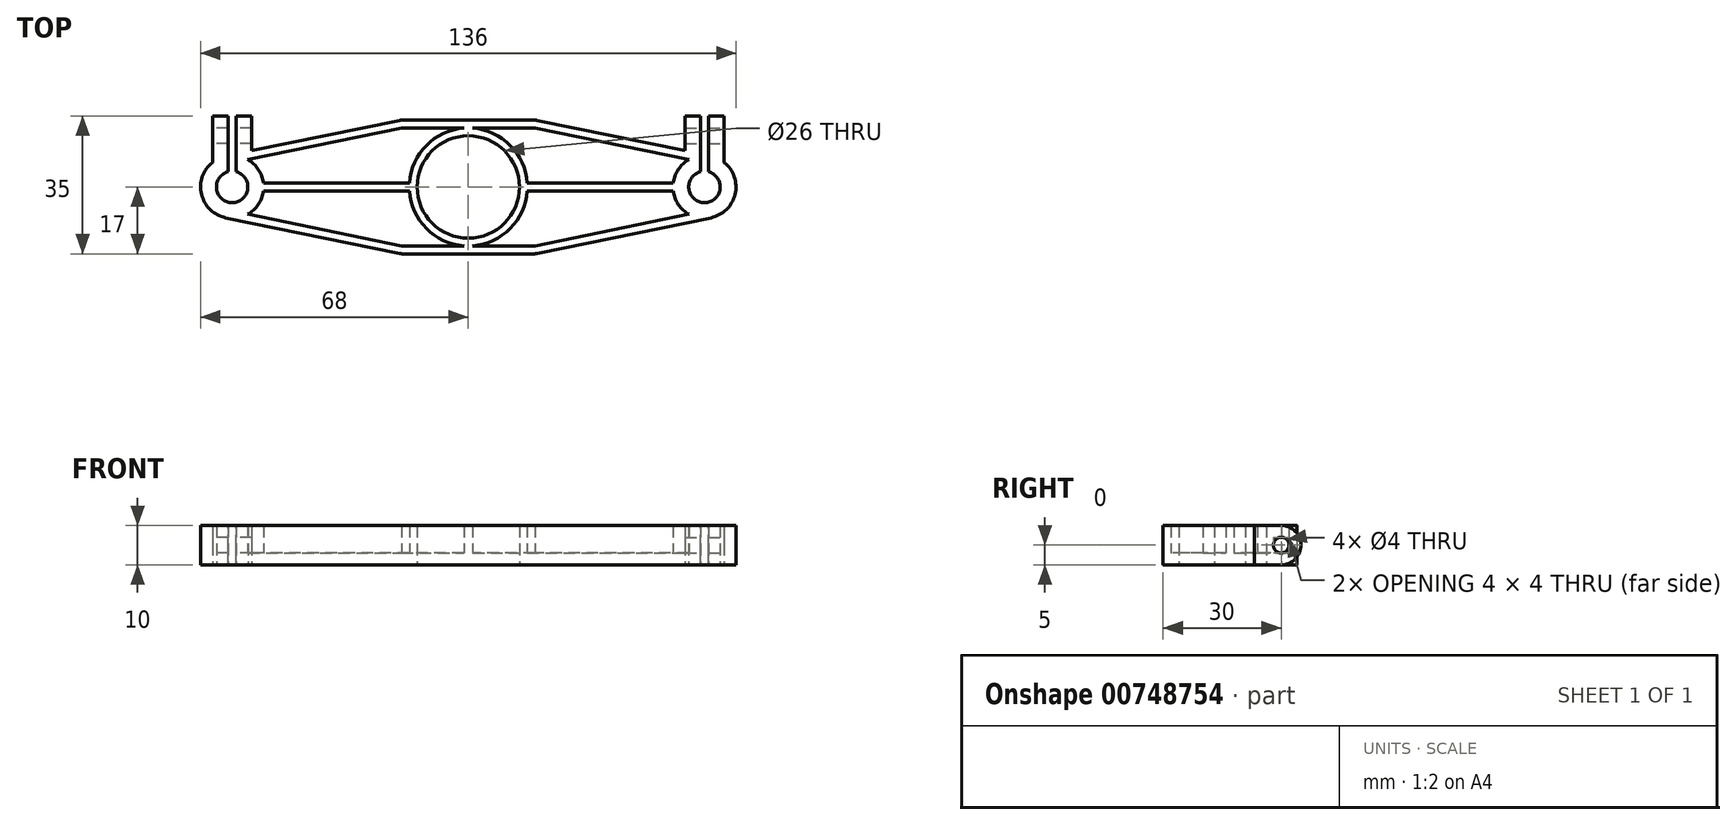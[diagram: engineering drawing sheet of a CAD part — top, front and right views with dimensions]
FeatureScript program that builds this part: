
annotation { "Feature Type Name" : "Feature", "Feature Type Description" : "" }
export const myFeature = defineFeature(function(context is Context, id is Id, definition is map)
    precondition{}
    {
        {
            var Q0;
            Q0=qCreatedBy(makeId("Top.planeOp"),FACE);
            var sketch = newSketch(context, id + "F0", { "sketchPlane" : qUnion([Q0])});
            skCircle(sketch, "E0", {"center": v(0, 0) * mm, "radius": 13 * mm});
            skCircle(sketch, "E1", {"center": v(-60, 0) * mm, "radius": 4 * mm});
            skLineSegment(sketch, "E2", {"start": v(0, -25) * mm, "end": v(0, 0) * mm});
            skCircle(sketch, "E3", {"center": v(-60, 0) * mm, "radius": 8 * mm});
            skLineSegment(sketch, "E4.bottom", {"start": v(-55, 0) * mm, "end": v(-65, 0) * mm});
            skLineSegment(sketch, "E4.top", {"start": v(-55, 18) * mm, "end": v(-65, 18) * mm});
            skLineSegment(sketch, "E4.left", {"start": v(-55, 0) * mm, "end": v(-55, 18) * mm});
            skLineSegment(sketch, "E4.right", {"start": v(-65, 0) * mm, "end": v(-65, 18) * mm});
            skLineSegment(sketch, "E5.bottom", {"start": v(-59, 18) * mm, "end": v(-61, 18) * mm});
            skLineSegment(sketch, "E5.top", {"start": v(-59, 0) * mm, "end": v(-61, 0) * mm});
            skLineSegment(sketch, "E5.left", {"start": v(-59, 18) * mm, "end": v(-59, 0) * mm});
            skLineSegment(sketch, "E5.right", {"start": v(-61, 18) * mm, "end": v(-61, 0) * mm});
            skCircle(sketch, "E6", {"center": v(0, 0) * mm, "radius": 15 * mm});
            skLineSegment(sketch, "E7.bottom", {"start": v(17, 17) * mm, "end": v(-17, 17) * mm});
            skLineSegment(sketch, "E7.top", {"start": v(17, -17) * mm, "end": v(-17, -17) * mm});
            skLineSegment(sketch, "E7.left", {"start": v(17, 17) * mm, "end": v(17, -17) * mm});
            skLineSegment(sketch, "E7.right", {"start": v(-17, 17) * mm, "end": v(-17, -17) * mm});
            skLineSegment(sketch, "E8", {"start": v(-61.6, 7.84) * mm, "end": v(-17, 17) * mm});
            skLineSegment(sketch, "E9", {"start": v(-61.6, -7.84) * mm, "end": v(-17, -17) * mm});
            skLineSegment(sketch, "E10", {"start": v(-17, 14.96) * mm, "end": v(-56.02, 6.94) * mm});
            skLineSegment(sketch, "E11", {"start": v(0, 0) * mm, "end": v(0, 17) * mm});
            skLineSegment(sketch, "E12", {"start": v(-17, -14.96) * mm, "end": v(-56.02, -6.94) * mm});
            skLineSegment(sketch, "E13", {"start": v(-17, 14.96) * mm, "end": v(0, 14.96) * mm});
            skLineSegment(sketch, "E14", {"start": v(-17, -14.96) * mm, "end": v(0, -14.96) * mm});
            skLineSegment(sketch, "E15", {"start": v(-60, 0) * mm, "end": v(0, 0) * mm, "construction": true});
            skLineSegment(sketch, "E16", {"start": v(-52.06, 1) * mm, "end": v(-14.97, 1) * mm});
            skLineSegment(sketch, "E17", {"start": v(-14.97, -1) * mm, "end": v(-52.06, -1) * mm});
            skSolve(sketch);
        }
        {
            var Q0;
            {var subQ0=sQuery(id+"F0.wireOp",EDGE,"E4.left");var subQ1=sQuery(id+"F0.wireOp",EDGE,"E4.top");var subQ2=makeQuery(id+"F0.imprint","INTERSECT",VERTEX,{"derivedFrom":[subQ1,subQ0]});Q0=makeQuery(id+"F0.imprint","IMPRINT",FACE,{"disambiguationData":[TD([[makeQuery(id+"F0.imprint","IMPRINT",EDGE,{"disambiguationData":[TD([[subQ2,1.0]])],"derivedFrom":subQ0}),1.0]])]});}
            var Q1;
            {var subQ5=sQuery(id+"F0.wireOp",EDGE,"E10");var subQ6=sQuery(id+"F0.wireOp",EDGE,"E3");var subQ7=makeQuery(id+"F0.imprint","INTERSECT",VERTEX,{"derivedFrom":[subQ6,subQ5]});Q1=makeQuery(id+"F0.imprint","IMPRINT",FACE,{"disambiguationData":[TD([[makeQuery(id+"F0.imprint","IMPRINT",EDGE,{"disambiguationData":[TD([[subQ7,-1.0]])],"derivedFrom":subQ6}),-1.0]])]});}
            var Q2;
            {var subQ3=sQuery(id+"F0.wireOp",EDGE,"E1");var subQ8=sQuery(id+"F0.wireOp",EDGE,"E5.left");var subQ10=makeQuery(id+"F0.imprint","INTERSECT",VERTEX,{"derivedFrom":[subQ3,subQ8]});Q2=makeQuery(id+"F0.imprint","IMPRINT",FACE,{"disambiguationData":[TD([[makeQuery(id+"F0.imprint","IMPRINT",EDGE,{"disambiguationData":[TD([[subQ10,1.0]])],"derivedFrom":subQ3}),-1.0]])]});}
            var Q3;
            {var subQ3=sQuery(id+"F0.wireOp",EDGE,"E1");var subQ7=sQuery(id+"F0.wireOp",EDGE,"E5.right");var subQ9=makeQuery(id+"F0.imprint","INTERSECT",VERTEX,{"derivedFrom":[subQ3,subQ7]});Q3=makeQuery(id+"F0.imprint","IMPRINT",FACE,{"disambiguationData":[TD([[makeQuery(id+"F0.imprint","IMPRINT",EDGE,{"disambiguationData":[TD([[subQ9,-1.0]])],"derivedFrom":subQ3}),-1.0]])]});}
            var Q4;
            {var subQ0=sQuery(id+"F0.wireOp",EDGE,"E4.right");var subQ1=sQuery(id+"F0.wireOp",EDGE,"E3");var subQ2=makeQuery(id+"F0.imprint","INTERSECT",VERTEX,{"derivedFrom":[subQ1,subQ0]});Q4=makeQuery(id+"F0.imprint","IMPRINT",FACE,{"disambiguationData":[TD([[makeQuery(id+"F0.imprint","IMPRINT",EDGE,{"disambiguationData":[TD([[subQ2,1.0]])],"derivedFrom":subQ1}),-1.0]])]});}
            var Q5;
            {var subQ5=sQuery(id+"F0.wireOp",EDGE,"E4.bottom");var subQ6=sQuery(id+"F0.wireOp",EDGE,"E1");var subQ7=makeQuery(id+"F0.imprint","INTERSECT",VERTEX,{"disambiguationData":[OD(0.0)],"derivedFrom":[subQ6,subQ5]});Q5=makeQuery(id+"F0.imprint","IMPRINT",FACE,{"disambiguationData":[TD([[makeQuery(id+"F0.imprint","IMPRINT",EDGE,{"disambiguationData":[TD([[subQ7,1.0]])],"derivedFrom":subQ6}),-1.0]])]});}
            var Q6;
            {var subQ0=sQuery(id+"F0.wireOp",EDGE,"E12");Q6=makeQuery(id+"F0.imprint","IMPRINT",FACE,{"disambiguationData":[TD([[makeQuery(id+"F0.imprint","IMPRINT",EDGE,{"derivedFrom":subQ0}),-1.0]])]});}
            var Q7;
            {var subQ5=sQuery(id+"F0.wireOp",EDGE,"E16");var subQ7=sQuery(id+"F0.wireOp",EDGE,"E3");var subQ9=makeQuery(id+"F0.imprint","INTERSECT",VERTEX,{"derivedFrom":[subQ7,subQ5]});Q7=makeQuery(id+"F0.imprint","IMPRINT",FACE,{"disambiguationData":[TD([[makeQuery(id+"F0.imprint","IMPRINT",EDGE,{"disambiguationData":[TD([[subQ9,-1.0]])],"derivedFrom":subQ7}),-1.0]])]});}
            var Q8;
            {var subQ0=sQuery(id+"F0.wireOp",EDGE,"E8");var subQ1=sQuery(id+"F0.wireOp",EDGE,"E4.left");var subQ2=makeQuery(id+"F0.imprint","INTERSECT",VERTEX,{"derivedFrom":[subQ1,subQ0]});Q8=makeQuery(id+"F0.imprint","IMPRINT",FACE,{"disambiguationData":[TD([[makeQuery(id+"F0.imprint","IMPRINT",EDGE,{"disambiguationData":[TD([[subQ2,1.0]])],"derivedFrom":subQ1}),-1.0]])]});}
            var Q9;
            {var subQ0=sQuery(id+"F0.wireOp",EDGE,"E16");var subQ1=sQuery(id+"F0.wireOp",EDGE,"E3");var subQ2=makeQuery(id+"F0.imprint","INTERSECT",VERTEX,{"derivedFrom":[subQ1,subQ0]});Q9=makeQuery(id+"F0.imprint","IMPRINT",FACE,{"disambiguationData":[TD([[makeQuery(id+"F0.imprint","IMPRINT",EDGE,{"disambiguationData":[TD([[subQ2,1.0]])],"derivedFrom":subQ1}),-1.0]])]});}
            var Q10;
            {var subQ0=sQuery(id+"F0.wireOp",EDGE,"E9");Q10=makeQuery(id+"F0.imprint","IMPRINT",FACE,{"disambiguationData":[TD([[makeQuery(id+"F0.imprint","IMPRINT",EDGE,{"derivedFrom":subQ0}),1.0]])]});}
            var Q11;
            {var subQ0=sQuery(id+"F0.wireOp",EDGE,"E14");Q11=makeQuery(id+"F0.imprint","IMPRINT",FACE,{"disambiguationData":[TD([[makeQuery(id+"F0.imprint","IMPRINT",EDGE,{"derivedFrom":subQ0}),-1.0]])]});}
            var Q12;
            {var subQ0=sQuery(id+"F0.wireOp",EDGE,"E14");Q12=makeQuery(id+"F0.imprint","IMPRINT",FACE,{"disambiguationData":[TD([[makeQuery(id+"F0.imprint","IMPRINT",EDGE,{"derivedFrom":subQ0}),1.0]])]});}
            var Q13;
            {var subQ5=sQuery(id+"F0.wireOp",EDGE,"E2");var subQ6=sQuery(id+"F0.wireOp",EDGE,"E0");var subQ7=makeQuery(id+"F0.imprint","INTERSECT",VERTEX,{"derivedFrom":[subQ6,subQ5]});Q13=makeQuery(id+"F0.imprint","IMPRINT",FACE,{"disambiguationData":[TD([[makeQuery(id+"F0.imprint","IMPRINT",EDGE,{"disambiguationData":[TD([[subQ7,1.0]])],"derivedFrom":subQ6}),-1.0]])]});}
            var Q14;
            {var subQ0=sQuery(id+"F0.wireOp",EDGE,"E16");var subQ1=sQuery(id+"F0.wireOp",EDGE,"E6");var subQ2=makeQuery(id+"F0.imprint","INTERSECT",VERTEX,{"derivedFrom":[subQ1,subQ0]});Q14=makeQuery(id+"F0.imprint","IMPRINT",FACE,{"disambiguationData":[TD([[makeQuery(id+"F0.imprint","IMPRINT",EDGE,{"disambiguationData":[TD([[subQ2,-1.0]])],"derivedFrom":subQ1}),-1.0]])]});}
            var Q15;
            {var subQ0=sQuery(id+"F0.wireOp",EDGE,"E13");Q15=makeQuery(id+"F0.imprint","IMPRINT",FACE,{"disambiguationData":[TD([[makeQuery(id+"F0.imprint","IMPRINT",EDGE,{"derivedFrom":subQ0}),-1.0]])]});}
            var Q16;
            {var subQ5=sQuery(id+"F0.wireOp",EDGE,"E13");Q16=makeQuery(id+"F0.imprint","IMPRINT",FACE,{"disambiguationData":[TD([[makeQuery(id+"F0.imprint","IMPRINT",EDGE,{"derivedFrom":subQ5}),1.0]])]});}
            var Q17;
            {var subQ0=sQuery(id+"F0.wireOp",EDGE,"E10");var subQ1=sQuery(id+"F0.wireOp",EDGE,"E3");var subQ2=makeQuery(id+"F0.imprint","INTERSECT",VERTEX,{"derivedFrom":[subQ1,subQ0]});Q17=makeQuery(id+"F0.imprint","IMPRINT",FACE,{"disambiguationData":[TD([[makeQuery(id+"F0.imprint","IMPRINT",EDGE,{"disambiguationData":[TD([[subQ2,1.0]])],"derivedFrom":subQ1}),-1.0]])]});}
            extrude(context, id + "F1", {"entities" : qUnion([Q0, Q1, Q2, Q3, Q4, Q5, Q6, Q7, Q8, Q9, Q10, Q11, Q12, Q13, Q14, Q15, Q16, Q17]), "depth" : 3 * mm, "offsetDistance" : 25 * mm});
        }
        {
            var Q0;
            {var subQ0=sQuery(id+"F0.wireOp",EDGE,"E14");Q0=makeQuery(id+"F0.imprint","IMPRINT",FACE,{"disambiguationData":[TD([[makeQuery(id+"F0.imprint","IMPRINT",EDGE,{"derivedFrom":subQ0}),-1.0]])]});}
            var Q1;
            {var subQ0=sQuery(id+"F0.wireOp",EDGE,"E9");Q1=makeQuery(id+"F0.imprint","IMPRINT",FACE,{"disambiguationData":[TD([[makeQuery(id+"F0.imprint","IMPRINT",EDGE,{"derivedFrom":subQ0}),1.0]])]});}
            var Q2;
            {var subQ5=sQuery(id+"F0.wireOp",EDGE,"E2");var subQ6=sQuery(id+"F0.wireOp",EDGE,"E0");var subQ7=makeQuery(id+"F0.imprint","INTERSECT",VERTEX,{"derivedFrom":[subQ6,subQ5]});Q2=makeQuery(id+"F0.imprint","IMPRINT",FACE,{"disambiguationData":[TD([[makeQuery(id+"F0.imprint","IMPRINT",EDGE,{"disambiguationData":[TD([[subQ7,1.0]])],"derivedFrom":subQ6}),-1.0]])]});}
            var Q3;
            {var subQ5=sQuery(id+"F0.wireOp",EDGE,"E13");Q3=makeQuery(id+"F0.imprint","IMPRINT",FACE,{"disambiguationData":[TD([[makeQuery(id+"F0.imprint","IMPRINT",EDGE,{"derivedFrom":subQ5}),1.0]])]});}
            var Q4;
            {var subQ0=sQuery(id+"F0.wireOp",EDGE,"E8");var subQ1=sQuery(id+"F0.wireOp",EDGE,"E4.left");var subQ2=makeQuery(id+"F0.imprint","INTERSECT",VERTEX,{"derivedFrom":[subQ1,subQ0]});Q4=makeQuery(id+"F0.imprint","IMPRINT",FACE,{"disambiguationData":[TD([[makeQuery(id+"F0.imprint","IMPRINT",EDGE,{"disambiguationData":[TD([[subQ2,1.0]])],"derivedFrom":subQ1}),-1.0]])]});}
            var Q5;
            {var subQ5=sQuery(id+"F0.wireOp",EDGE,"E10");var subQ6=sQuery(id+"F0.wireOp",EDGE,"E3");var subQ7=makeQuery(id+"F0.imprint","INTERSECT",VERTEX,{"derivedFrom":[subQ6,subQ5]});Q5=makeQuery(id+"F0.imprint","IMPRINT",FACE,{"disambiguationData":[TD([[makeQuery(id+"F0.imprint","IMPRINT",EDGE,{"disambiguationData":[TD([[subQ7,-1.0]])],"derivedFrom":subQ6}),-1.0]])]});}
            var Q6;
            {var subQ5=sQuery(id+"F0.wireOp",EDGE,"E4.bottom");var subQ6=sQuery(id+"F0.wireOp",EDGE,"E1");var subQ7=makeQuery(id+"F0.imprint","INTERSECT",VERTEX,{"disambiguationData":[OD(0.0)],"derivedFrom":[subQ6,subQ5]});Q6=makeQuery(id+"F0.imprint","IMPRINT",FACE,{"disambiguationData":[TD([[makeQuery(id+"F0.imprint","IMPRINT",EDGE,{"disambiguationData":[TD([[subQ7,1.0]])],"derivedFrom":subQ6}),-1.0]])]});}
            var Q7;
            {var subQ3=sQuery(id+"F0.wireOp",EDGE,"E1");var subQ8=sQuery(id+"F0.wireOp",EDGE,"E5.left");var subQ10=makeQuery(id+"F0.imprint","INTERSECT",VERTEX,{"derivedFrom":[subQ3,subQ8]});Q7=makeQuery(id+"F0.imprint","IMPRINT",FACE,{"disambiguationData":[TD([[makeQuery(id+"F0.imprint","IMPRINT",EDGE,{"disambiguationData":[TD([[subQ10,1.0]])],"derivedFrom":subQ3}),-1.0]])]});}
            var Q8;
            {var subQ3=sQuery(id+"F0.wireOp",EDGE,"E1");var subQ7=sQuery(id+"F0.wireOp",EDGE,"E5.right");var subQ9=makeQuery(id+"F0.imprint","INTERSECT",VERTEX,{"derivedFrom":[subQ3,subQ7]});Q8=makeQuery(id+"F0.imprint","IMPRINT",FACE,{"disambiguationData":[TD([[makeQuery(id+"F0.imprint","IMPRINT",EDGE,{"disambiguationData":[TD([[subQ9,-1.0]])],"derivedFrom":subQ3}),-1.0]])]});}
            var Q9;
            {var subQ0=sQuery(id+"F0.wireOp",EDGE,"E4.right");var subQ1=sQuery(id+"F0.wireOp",EDGE,"E3");var subQ2=makeQuery(id+"F0.imprint","INTERSECT",VERTEX,{"derivedFrom":[subQ1,subQ0]});Q9=makeQuery(id+"F0.imprint","IMPRINT",FACE,{"disambiguationData":[TD([[makeQuery(id+"F0.imprint","IMPRINT",EDGE,{"disambiguationData":[TD([[subQ2,1.0]])],"derivedFrom":subQ1}),-1.0]])]});}
            var Q10;
            {var subQ0=sQuery(id+"F0.wireOp",EDGE,"E4.left");var subQ1=sQuery(id+"F0.wireOp",EDGE,"E4.top");var subQ2=makeQuery(id+"F0.imprint","INTERSECT",VERTEX,{"derivedFrom":[subQ1,subQ0]});Q10=makeQuery(id+"F0.imprint","IMPRINT",FACE,{"disambiguationData":[TD([[makeQuery(id+"F0.imprint","IMPRINT",EDGE,{"disambiguationData":[TD([[subQ2,1.0]])],"derivedFrom":subQ0}),1.0]])]});}
            var Q11;
            {var subQ0=sQuery(id+"F0.wireOp",EDGE,"E16");var subQ1=sQuery(id+"F0.wireOp",EDGE,"E3");var subQ2=makeQuery(id+"F0.imprint","INTERSECT",VERTEX,{"derivedFrom":[subQ1,subQ0]});Q11=makeQuery(id+"F0.imprint","IMPRINT",FACE,{"disambiguationData":[TD([[makeQuery(id+"F0.imprint","IMPRINT",EDGE,{"disambiguationData":[TD([[subQ2,1.0]])],"derivedFrom":subQ1}),-1.0]])]});}
            var Q12;
            {var subQ0=sQuery(id+"F0.wireOp",EDGE,"E16");var subQ1=sQuery(id+"F0.wireOp",EDGE,"E6");var subQ2=makeQuery(id+"F0.imprint","INTERSECT",VERTEX,{"derivedFrom":[subQ1,subQ0]});Q12=makeQuery(id+"F0.imprint","IMPRINT",FACE,{"disambiguationData":[TD([[makeQuery(id+"F0.imprint","IMPRINT",EDGE,{"disambiguationData":[TD([[subQ2,-1.0]])],"derivedFrom":subQ1}),-1.0]])]});}
            var Q13;
            {var subQ3=sQuery(id+"F0.wireOp",EDGE,"E13");var subQ5=sQuery(id+"F0.wireOp",EDGE,"E6");var subQ6=makeQuery(id+"F0.imprint","INTERSECT",VERTEX,{"derivedFrom":[subQ5,subQ3]});Q13=makeQuery(id+"F0.imprint","IMPRINT",FACE,{"disambiguationData":[TD([[makeQuery(id+"F0.imprint","IMPRINT",EDGE,{"disambiguationData":[TD([[subQ6,1.0]])],"derivedFrom":subQ5}),-1.0]])]});}
            var Q14;
            {var subQ1=sQuery(id+"F0.wireOp",EDGE,"E7.top");var subQ3=sQuery(id+"F0.wireOp",EDGE,"E2");var subQ4=makeQuery(id+"F0.imprint","INTERSECT",VERTEX,{"derivedFrom":[subQ3,subQ1]});Q14=makeQuery(id+"F0.imprint","IMPRINT",FACE,{"disambiguationData":[TD([[makeQuery(id+"F0.imprint","IMPRINT",EDGE,{"disambiguationData":[TD([[subQ4,-1.0]])],"derivedFrom":subQ3}),1.0]])]});}
            var Q15;
            {var subQ0=sQuery(id+"F0.wireOp",EDGE,"E8");var subQ1=sQuery(id+"F0.wireOp",EDGE,"E3");var subQ2=makeQuery(id+"F0.imprint","INTERSECT",VERTEX,{"derivedFrom":[subQ1,subQ0]});Q15=makeQuery(id+"F0.imprint","IMPRINT",FACE,{"disambiguationData":[TD([[makeQuery(id+"F0.imprint","IMPRINT",EDGE,{"disambiguationData":[TD([[subQ2,1.0]])],"derivedFrom":subQ1}),-1.0]])]});}
            extrude(context, id + "F2", {"entities" : qUnion([Q0, Q1, Q2, Q3, Q4, Q5, Q6, Q7, Q8, Q9, Q10, Q11, Q12, Q13, Q14, Q15]), "operationType" : NewBodyOperationType.ADD, "depth" : 10 * mm, "offsetDistance" : 25 * mm});
        }
        {
            var Q0;
            {var subQ0=sQuery(id+"F0.wireOp",EDGE,"E4.right");Q0=makeQuery(id+"F2.boolean.opBoolean","MERGE",FACE,{"derivedFrom":[makeQuery(id+"F1.opExtrude","SWEPT_FACE",FACE,{"disambiguationData":[OSD([subQ0])]}),makeQuery(id+"F2.opExtrude","SWEPT_FACE",FACE,{"disambiguationData":[OSD([subQ0])]})]});}
            var sketch = newSketch(context, id + "F3", { "sketchPlane" : qUnion([Q0])});
            skLineSegment(sketch, "E18.0", {"start": v(-18, 10) * mm, "end": v(-18, 0) * mm});
            skLineSegment(sketch, "E18.1", {"start": v(-6.24, 10) * mm, "end": v(-18, 10) * mm});
            skCircle(sketch, "E19", {"center": v(-13, 5) * mm, "radius": 2 * mm});
            skSolve(sketch);
        }
        {
            var Q0;
            Q0=makeQuery(id+"F3.imprint","IMPRINT",FACE,{"disambiguationData":[TD([[makeQuery(id+"F3.imprint","IMPRINT",EDGE,{"derivedFrom":sQuery(id+"F3.wireOp",EDGE,"E19")}),1.0]])]});
            extrude(context, id + "F4", {"entities" : qUnion([Q0]), "operationType" : NewBodyOperationType.REMOVE, "oppositeDirection" : true, "depth" : 12 * mm, "offsetDistance" : 25 * mm});
        }
        {
            var Q0;
            {var subQ0=sQuery(id+"F0.wireOp",EDGE,"E4.top");Q0=makeQuery(id+"F1.opExtrude","CAP_EDGE",EDGE,{"disambiguationData":[OSD([subQ0]),TDD([makeQuery(id+"F0.imprint","IMPRINT",EDGE,{"disambiguationData":[TD([[makeQuery(id+"F0.imprint","INTERSECT",VERTEX,{"derivedFrom":[subQ0,sQuery(id+"F0.wireOp",EDGE,"E4.right")]}),1.0]])],"derivedFrom":subQ0})])],"isStart":true});}
            var Q1;
            {var subQ0=sQuery(id+"F0.wireOp",EDGE,"E4.top");Q1=makeQuery(id+"F1.opExtrude","CAP_EDGE",EDGE,{"disambiguationData":[OSD([subQ0]),TDD([makeQuery(id+"F0.imprint","IMPRINT",EDGE,{"disambiguationData":[TD([[makeQuery(id+"F0.imprint","INTERSECT",VERTEX,{"derivedFrom":[subQ0,sQuery(id+"F0.wireOp",EDGE,"E4.left")]}),-1.0]])],"derivedFrom":subQ0})])],"isStart":true});}
            var Q2;
            {var subQ0=sQuery(id+"F0.wireOp",EDGE,"E4.top");Q2=makeQuery(id+"F2.opExtrude","CAP_EDGE",EDGE,{"disambiguationData":[OSD([subQ0]),TDD([makeQuery(id+"F0.imprint","IMPRINT",EDGE,{"disambiguationData":[TD([[makeQuery(id+"F0.imprint","INTERSECT",VERTEX,{"derivedFrom":[subQ0,sQuery(id+"F0.wireOp",EDGE,"E4.left")]}),-1.0]])],"derivedFrom":subQ0})])],"isStart":false});}
            var Q3;
            {var subQ0=sQuery(id+"F0.wireOp",EDGE,"E4.top");Q3=makeQuery(id+"F2.opExtrude","CAP_EDGE",EDGE,{"disambiguationData":[OSD([subQ0]),TDD([makeQuery(id+"F0.imprint","IMPRINT",EDGE,{"disambiguationData":[TD([[makeQuery(id+"F0.imprint","INTERSECT",VERTEX,{"derivedFrom":[subQ0,sQuery(id+"F0.wireOp",EDGE,"E4.right")]}),1.0]])],"derivedFrom":subQ0})])],"isStart":false});}
            var Q4;
            {var subQ0=sQuery(id+"F0.wireOp",EDGE,"E8");var subQ1=sQuery(id+"F0.wireOp",EDGE,"E7.right");var subQ2=sQuery(id+"F0.wireOp",EDGE,"E7.bottom");Q4=makeQuery(id+"F2.boolean.opBoolean","MERGE",EDGE,{"derivedFrom":[makeQuery(id+"F1.opExtrude","SWEPT_EDGE",EDGE,{"disambiguationData":[OSD([subQ2,subQ1,subQ0])]}),makeQuery(id+"F2.opExtrude","SWEPT_EDGE",EDGE,{"disambiguationData":[OSD([subQ2,subQ1,subQ0])]})]});}
            var Q5;
            {var subQ0=sQuery(id+"F0.wireOp",EDGE,"E9");var subQ1=sQuery(id+"F0.wireOp",EDGE,"E7.right");var subQ2=sQuery(id+"F0.wireOp",EDGE,"E7.top");Q5=makeQuery(id+"F2.boolean.opBoolean","MERGE",EDGE,{"derivedFrom":[makeQuery(id+"F1.opExtrude","SWEPT_EDGE",EDGE,{"disambiguationData":[OSD([subQ2,subQ1,subQ0])]}),makeQuery(id+"F2.opExtrude","SWEPT_EDGE",EDGE,{"disambiguationData":[OSD([subQ2,subQ1,subQ0])]})]});}
            fillet(context, id + "F5", {"entities" : qUnion([Q0, Q1, Q2, Q3, Q4, Q5]), "radius" : 5 * mm, "tangentPropagation" : true, "allowEdgeOverflow" : false});
        }
        {
            var Q0;
            Q0=makeQuery(id+"F1.opExtrude","SWEPT_BODY",BODY,{"disambiguationData":[OSD([sQuery(id+"F0.wireOp",EDGE,"E0"),sQuery(id+"F0.wireOp",EDGE,"E1"),sQuery(id+"F0.wireOp",EDGE,"E2"),sQuery(id+"F0.wireOp",EDGE,"E3"),sQuery(id+"F0.wireOp",EDGE,"E4.top"),sQuery(id+"F0.wireOp",EDGE,"E4.left"),sQuery(id+"F0.wireOp",EDGE,"E4.right"),sQuery(id+"F0.wireOp",EDGE,"E5.left"),sQuery(id+"F0.wireOp",EDGE,"E5.right"),sQuery(id+"F0.wireOp",EDGE,"E6"),sQuery(id+"F0.wireOp",EDGE,"E7.right"),sQuery(id+"F0.wireOp",EDGE,"E8"),sQuery(id+"F0.wireOp",EDGE,"E9"),sQuery(id+"F0.wireOp",EDGE,"E11"),sQuery(id+"F0.wireOp",EDGE,"E13"),sQuery(id+"F0.wireOp",EDGE,"E14")])]});
            var Q1;
            {var subQ0=sQuery(id+"F0.wireOp",EDGE,"E2");Q1=makeQuery(id+"F2.boolean.opBoolean","MERGE",FACE,{"derivedFrom":[makeQuery(id+"F1.opExtrude","SWEPT_FACE",FACE,{"disambiguationData":[OSD([subQ0])]}),makeQuery(id+"F2.opExtrude","SWEPT_FACE",FACE,{"disambiguationData":[OSD([subQ0])]})]});}
            mirror(context, id + "F6", {"operationType" : NewBodyOperationType.ADD, "entities" : qUnion([Q0]), "mirrorPlane" : qUnion([Q1])});
        }
    });
